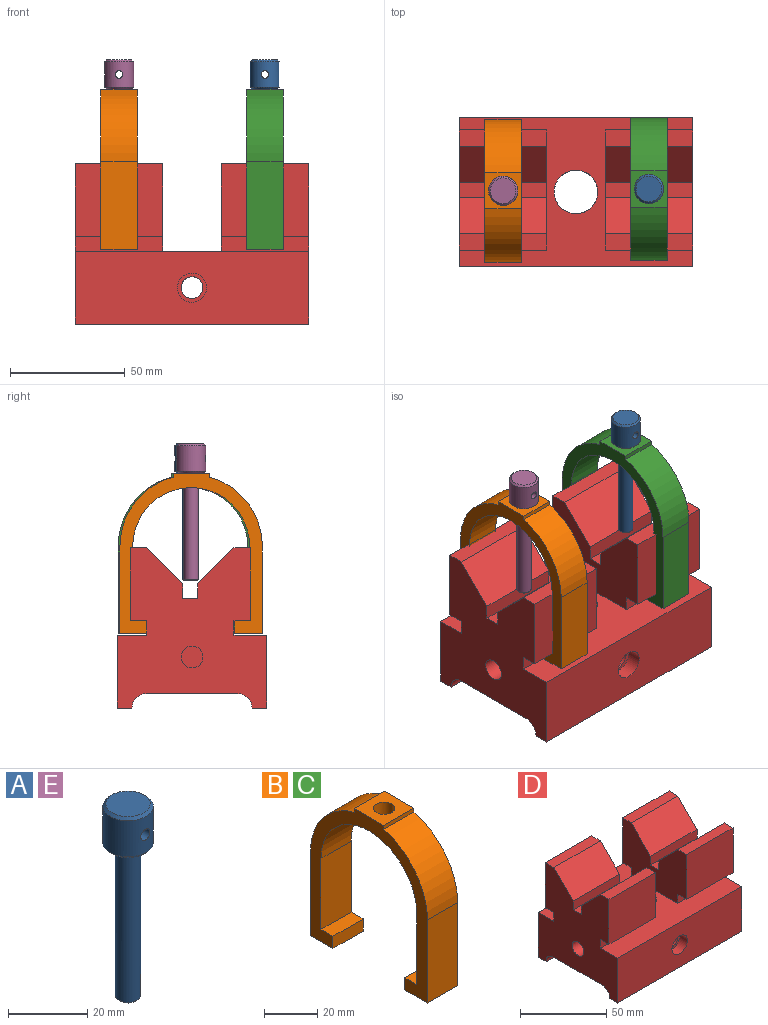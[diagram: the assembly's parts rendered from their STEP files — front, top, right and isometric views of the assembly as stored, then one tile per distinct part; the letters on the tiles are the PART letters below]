
ASSEMBLY  parts=5 mates=4
PART A: 9 faces, bbox 12.7x12.7x59.7 mm
  f0: plane 11.18x11.18mm, normal (0,0,1), area 98.1mm2, adj f6
  f1: plane 5.33x5.33mm, normal (0,0,-1), area 22.3mm2, adj f8
  f2: cylinder r=3.17mm len=46.48mm, axis (0,0,-1), area 927.3mm2, adj f3,f8
  f3: plane 11.18x11.18mm, normal (0,0,-1), area 66.4mm2, adj f2,f5
  f4: cylinder r=6.35mm len=12.7mm, axis (0,0,-1), area 428.6mm2, adj f5,f6,f7
  f5: cone r=5.59mm half-angle=45deg, axis (0,0,1), area 40.4mm2, adj f3,f4
  f6: cone r=6.35mm half-angle=45deg, axis (0,0,-1), area 40.4mm2, adj f0,f4
  f7: cylinder r=1.65mm len=12.7mm, axis (0,-1,0), area 129.5mm2, adj f4
  f8: cone r=2.67mm half-angle=45deg, axis (0,0,1), area 13.2mm2, adj f1,f2
PART B: 19 faces, bbox 16x62x69.9 mm
  f0: cylinder r=25.4mm len=50.8mm, axis (-1,0,0), area 1227.2mm2, adj f13,f14,f16,f17,f18
  f1: plane 16x5.59mm, normal (0,-1,0), area 89.4mm2, adj f2,f15,f16,f17
  f2: plane 16x11.94mm, normal (0,0,-1), area 191mm2, adj f1,f3,f16,f17
  f3: plane 38.1x16mm, normal (0,1,0), area 609.7mm2, adj f2,f4,f16,f17
  f4: cylinder r=30.99mm len=29.97mm, axis (-1,0,0), area 651.5mm2, adj f3,f5,f16,f17
  f5: plane 16x1.78mm, normal (0,1,0), area 28.5mm2, adj f4,f6,f16,f17
  f6: plane 16x15.75mm, normal (0,0,1), area 202.4mm2, adj f5,f7,f16,f17,f18
  f7: plane 16x1.78mm, normal (0,-1,0), area 28.5mm2, adj f6,f8,f16,f17
  f8: cylinder r=30.99mm len=29.97mm, axis (-1,0,0), area 651.5mm2, adj f7,f9,f16,f17
  f9: plane 38.1x16mm, normal (0,-1,0), area 609.7mm2, adj f8,f10,f16,f17
  f10: plane 16x11.94mm, normal (0,0,-1), area 191mm2, adj f9,f11,f16,f17
  f11: plane 16x5.59mm, normal (0,1,0), area 89.4mm2, adj f10,f12,f16,f17
  f12: plane 16x6.35mm, normal (0,0,1), area 101.6mm2, adj f11,f13,f16,f17
  f13: plane 32.51x16mm, normal (0,1,0), area 520.3mm2, adj f0,f12,f16,f17
  f14: plane 32.51x16mm, normal (0,-1,0), area 520.3mm2, adj f0,f15,f16,f17
  f15: plane 16x6.35mm, normal (0,0,1), area 101.6mm2, adj f1,f14,f16,f17
  f16: plane 69.85x61.98mm, normal (1,0,0), area 1009mm2, adj f0,f1,f2,f3,f4,f5,f6,f7
  f17: plane 69.85x61.98mm, normal (-1,0,0), area 1009mm2, adj f0,f1,f2,f3,f4,f5,f6,f7
  f18: cylinder r=3.98mm len=7.95mm, axis (0,0,1), area 162.5mm2, adj f0,f6
PART C: same geometry as B
PART D: 47 faces, bbox 101.6x65x69.9 mm
  f0: cylinder r=9.53mm len=25.4mm, axis (0,0,-1), area 1373mm2, adj f6,f9,f43,f44
  f1: plane 101.6x6.35mm, normal (0,0,-1), area 645.2mm2, adj f2,f3,f4,f8
  f2: plane 69.85x65.02mm, normal (-1,0,0), area 3187.6mm2, adj f1,f4,f5,f6,f7,f8,f9,f10
  f3: plane 69.85x65.02mm, normal (1,0,0), area 3187.6mm2, adj f1,f4,f5,f6,f7,f8,f9,f10
  f4: plane 101.6x31.75mm, normal (0,1,0), area 3154.5mm2, adj f1,f2,f3,f6,f43
  f5: plane 101.6x31.75mm, normal (0,-1,0), area 3099.1mm2, adj f2,f3,f6,f7,f46
  f6: plane 101.6x65.02mm, normal (0,0,1), area 3418.2mm2, adj f0,f2,f3,f4,f5,f22,f23,f24
  f7: plane 101.6x6.35mm, normal (0,0,-1), area 645.2mm2, adj f2,f3,f5,f10
  f8: cylinder r=6.35mm len=101.6mm, axis (1,0,0), area 1013.4mm2, adj f1,f2,f3,f9
  f9: plane 101.6x39.62mm, normal (0,0,-1), area 3740.8mm2, adj f0,f2,f3,f8,f10
  f10: cylinder r=6.35mm len=101.6mm, axis (1,0,0), area 1013.4mm2, adj f2,f3,f7,f9
  f11: plane 38.1x7.11mm, normal (0,0,-1), area 271mm2, adj f2,f12,f22,f23
  f12: plane 38.1x31.75mm, normal (0,1,0), area 1209.7mm2, adj f2,f11,f13,f22
  f13: plane 38.1x7.11mm, normal (0,0,1), area 271mm2, adj f2,f12,f14,f22
  f14: plane 38.1x15.75mm, normal (0,-0.71,0.71), area 848.5mm2, adj f2,f13,f15,f22
  f15: plane 38.1x6.35mm, normal (0,-1,0), area 241.9mm2, adj f2,f14,f16,f22
  f16: plane 38.1x6.6mm, normal (0,0,1), area 251.6mm2, adj f2,f15,f17,f22
  f17: plane 38.1x6.35mm, normal (0,1,0), area 241.9mm2, adj f2,f16,f18,f22
  f18: plane 38.1x15.75mm, normal (0,0.71,0.71), area 848.5mm2, adj f2,f17,f19,f22
  f19: plane 38.1x7.11mm, normal (0,0,1), area 271mm2, adj f2,f18,f20,f22
  f20: plane 38.1x31.75mm, normal (0,-1,0), area 1209.7mm2, adj f2,f19,f21,f22
  f21: plane 38.1x7.11mm, normal (0,0,-1), area 271mm2, adj f2,f20,f22,f24
  f22: plane 52.32x38.1mm, normal (1,0,0), area 1509.3mm2, adj f6,f11,f12,f13,f14,f15,f16,f17
  f23: plane 38.1x6.35mm, normal (0,1,0), area 241.9mm2, adj f2,f6,f11,f22
  f24: plane 38.1x6.35mm, normal (0,-1,0), area 241.9mm2, adj f2,f6,f21,f22
  f25: plane 38.1x6.35mm, normal (0,1,0), area 241.9mm2, adj f3,f6,f26,f38
  f26: plane 38.1x7.11mm, normal (0,0,-1), area 271mm2, adj f3,f25,f27,f38
  f27: plane 38.1x31.75mm, normal (0,1,0), area 1209.7mm2, adj f3,f26,f28,f38
  f28: plane 38.1x7.11mm, normal (0,0,1), area 271mm2, adj f3,f27,f29,f38
  f29: plane 38.1x15.75mm, normal (0,-0.71,0.71), area 848.5mm2, adj f3,f28,f30,f38
  f30: plane 38.1x6.35mm, normal (0,-1,0), area 241.9mm2, adj f3,f29,f31,f38
  f31: plane 38.1x6.6mm, normal (0,0,1), area 251.6mm2, adj f3,f30,f32,f38
  f32: plane 38.1x6.35mm, normal (0,1,0), area 241.9mm2, adj f3,f31,f33,f38
  f33: plane 38.1x15.75mm, normal (0,0.71,0.71), area 848.5mm2, adj f3,f32,f34,f38
  f34: plane 38.1x7.11mm, normal (0,0,1), area 271mm2, adj f3,f33,f35,f38
  f35: plane 38.1x31.75mm, normal (0,-1,0), area 1209.7mm2, adj f3,f34,f36,f38
  f36: plane 38.1x7.11mm, normal (0,0,-1), area 271mm2, adj f3,f35,f37,f38
  f37: plane 38.1x6.35mm, normal (0,-1,0), area 241.9mm2, adj f3,f6,f36,f38
  f38: plane 52.32x38.1mm, normal (-1,0,0), area 1509.3mm2, adj f6,f25,f26,f27,f28,f29,f30,f31
  f39: cylinder r=4.76mm len=15.88mm, axis (1,0,0), area 475mm2, adj f3,f40
  f40: plane 9.53x9.53mm, normal (1,0,0), area 71.3mm2, adj f39
  f41: cylinder r=4.76mm len=15.88mm, axis (-1,0,0), area 475mm2, adj f2,f42
  f42: plane 9.53x9.53mm, normal (-1,0,0), area 71.3mm2, adj f41
  f43: cylinder r=4.76mm len=24.26mm, axis (0,-1,0), area 706.6mm2, adj f0,f4
  f44: cylinder r=4.76mm len=17.91mm, axis (0,-1,0), area 516.6mm2, adj f0,f45
  f45: plane 12.7x12.7mm, normal (0,-1,0), area 55.4mm2, adj f44,f46
  f46: cylinder r=6.35mm len=12.7mm, axis (0,-1,0), area 253.4mm2, adj f5,f45
PART E: same geometry as A
PLACE A t=(29.92,89.48,-33.46)mm
PLACE B t=(-33.58,88.72,-56.32)mm
PLACE C t=(29.92,89.48,-56.32)mm
PLACE D t=(-1.83,88.34,-88.84)mm
PLACE E t=(-33.58,88.72,-33.46)mm
MATE slider C.f15 <-> D.f26  axis (0,0,1) through (29.92,111.71,-50.74)mm
MATE cylindrical A.f2 <-> C.f18  axis (0,0,-1) through (29.92,89.48,13.53)mm
MATE cylindrical E.f2 <-> B.f18  axis (0,0,-1) through (-33.58,88.72,13.53)mm
MATE slider B.f12 <-> D.f21  axis (0,0,1) through (-33.58,66.49,-50.74)mm
